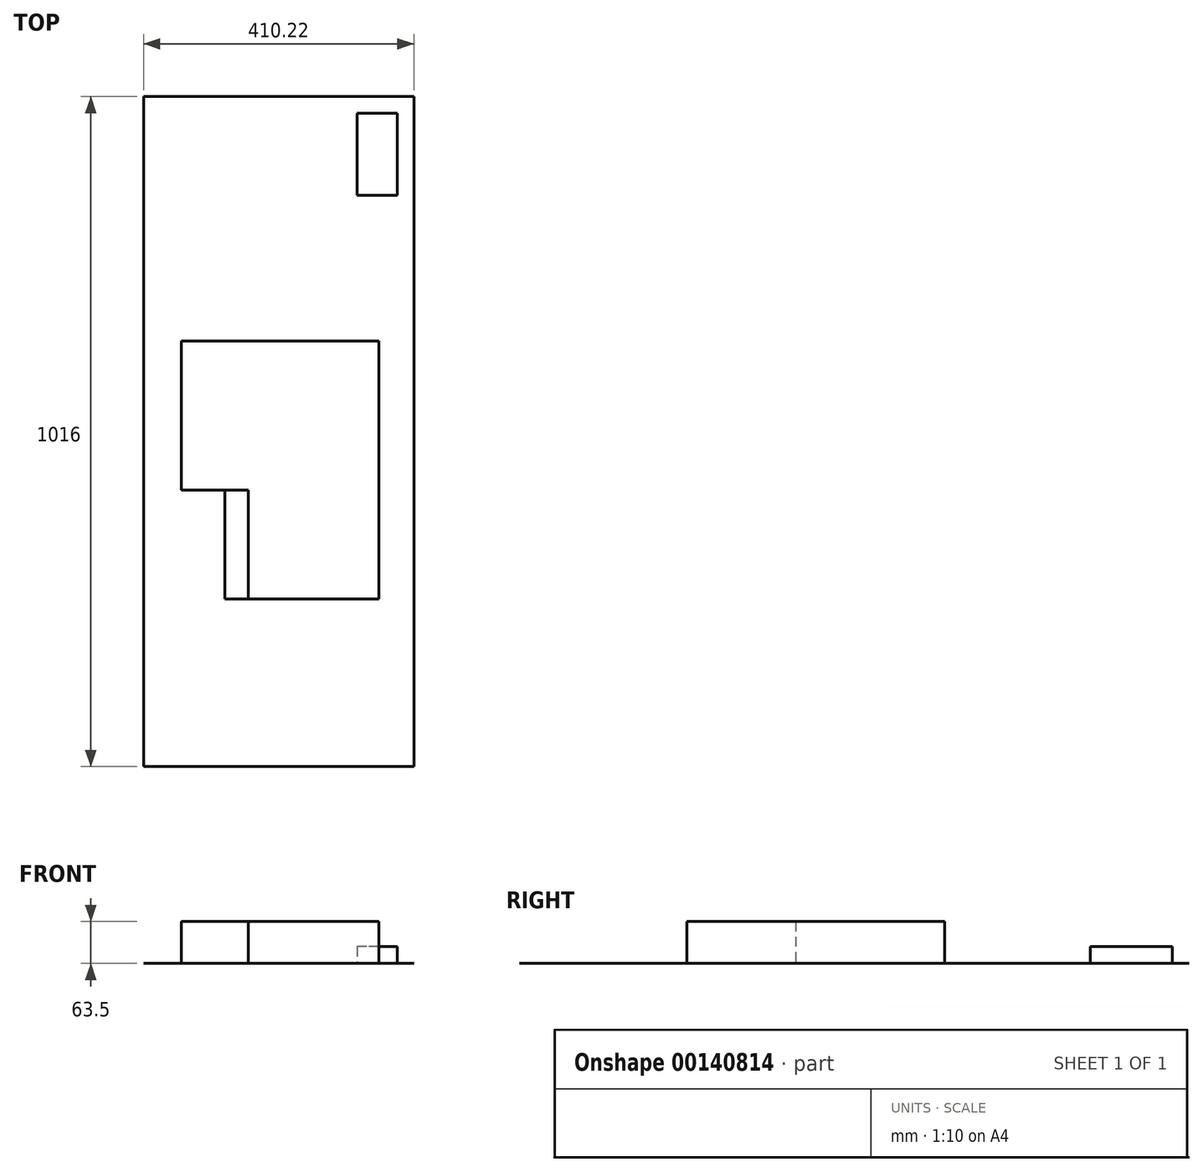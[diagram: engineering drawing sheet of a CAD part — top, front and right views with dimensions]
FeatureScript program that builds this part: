
annotation { "Feature Type Name" : "Feature", "Feature Type Description" : "" }
export const myFeature = defineFeature(function(context is Context, id is Id, definition is map)
    precondition{}
    {
        {
            var Q0;
            Q0=qCreatedBy(makeId("Top.planeOp"),FACE);
            var sketch = newSketch(context, id + "F0", { "sketchPlane" : qUnion([Q0])});
            skLineSegment(sketch, "E0.bottom", {"start": v(-205.1, 508) * mm, "end": v(205.1, 508) * mm});
            skLineSegment(sketch, "E0.top", {"start": v(-205.1, -508) * mm, "end": v(205.1, -508) * mm});
            skLineSegment(sketch, "E0.left", {"start": v(-205.1, 508) * mm, "end": v(-205.1, -508) * mm});
            skLineSegment(sketch, "E0.right", {"start": v(205.1, 508) * mm, "end": v(205.1, -508) * mm});
            skPoint(sketch, "E0.middle", {"position": v(0, 0) * mm});
            skSolve(sketch);
        }
        {
            var Q0;
            Q0=makeQuery(id+"F0.imprint","IMPRINT",FACE,{"disambiguationData":[TD([[makeQuery(id+"F0.imprint","IMPRINT",EDGE,{"derivedFrom":sQuery(id+"F0.wireOp",EDGE,"E0.bottom")}),-1.0]])]});
            var sketch = newSketch(context, id + "F1", { "sketchPlane" : qUnion([Q0])});
            skLineSegment(sketch, "E1.bottom", {"start": v(205.1, 508) * mm, "end": v(151.77, 508) * mm});
            skLineSegment(sketch, "E1.top", {"start": v(205.1, 137.16) * mm, "end": v(151.77, 137.16) * mm});
            skLineSegment(sketch, "E1.left", {"start": v(205.1, 508) * mm, "end": v(205.1, 137.16) * mm});
            skLineSegment(sketch, "E1.right", {"start": v(151.77, 508) * mm, "end": v(151.77, 137.16) * mm});
            skLineSegment(sketch, "E2.bottom", {"start": v(-205.1, 508) * mm, "end": v(-147.95, 508) * mm});
            skLineSegment(sketch, "E2.top", {"start": v(-205.1, 137.16) * mm, "end": v(-147.95, 137.16) * mm});
            skLineSegment(sketch, "E2.left", {"start": v(-205.1, 508) * mm, "end": v(-205.1, 137.16) * mm});
            skLineSegment(sketch, "E2.right", {"start": v(-147.95, 508) * mm, "end": v(-147.95, 137.16) * mm});
            skSolve(sketch);
        }
        {
            var Q0;
            Q0=makeQuery(id+"F0.imprint","IMPRINT",FACE,{"disambiguationData":[TD([[makeQuery(id+"F0.imprint","IMPRINT",EDGE,{"derivedFrom":sQuery(id+"F0.wireOp",EDGE,"E0.bottom")}),-1.0]])]});
            var sketch = newSketch(context, id + "F2", { "sketchPlane" : qUnion([Q0])});
            skLineSegment(sketch, "E3.bottom", {"start": v(151.77, 137.16) * mm, "end": v(-147.95, 137.16) * mm});
            skLineSegment(sketch, "E3.top", {"start": v(151.77, -254) * mm, "end": v(-147.95, -254) * mm});
            skLineSegment(sketch, "E3.left", {"start": v(151.77, 137.16) * mm, "end": v(151.77, -254) * mm});
            skLineSegment(sketch, "E3.right", {"start": v(-147.95, 137.16) * mm, "end": v(-147.95, -254) * mm});
            skLineSegment(sketch, "E4", {"start": v(151.77, -254) * mm, "end": v(-46.35, -254) * mm});
            skLineSegment(sketch, "E5", {"start": v(-46.35, -254) * mm, "end": v(-46.35, -88.9) * mm});
            skLineSegment(sketch, "E6", {"start": v(-46.35, -88.9) * mm, "end": v(-147.95, -88.9) * mm});
            skLineSegment(sketch, "E7", {"start": v(-81.91, -88.9) * mm, "end": v(-81.91, -254) * mm});
            skLineSegment(sketch, "E8", {"start": v(-81.91, -88.9) * mm, "end": v(-46.35, -88.9) * mm});
            skLineSegment(sketch, "E9", {"start": v(-46.35, -254) * mm, "end": v(-46.35, -508) * mm});
            skLineSegment(sketch, "E10", {"start": v(151.77, -254) * mm, "end": v(151.77, -508) * mm});
            skLineSegment(sketch, "E11", {"start": v(-46.35, -254) * mm, "end": v(-46.35, -299.72) * mm});
            skLineSegment(sketch, "E12", {"start": v(-46.35, -299.72) * mm, "end": v(-81.91, -254) * mm});
            skLineSegment(sketch, "E13", {"start": v(151.77, -254) * mm, "end": v(151.77, -299.72) * mm});
            skLineSegment(sketch, "E14", {"start": v(151.77, -299.72) * mm, "end": v(187.33, -254) * mm});
            skLineSegment(sketch, "E15", {"start": v(187.33, -254) * mm, "end": v(187.33, -79.8) * mm});
            skLineSegment(sketch, "E16", {"start": v(187.33, -79.8) * mm, "end": v(151.77, -79.8) * mm});
            skSolve(sketch);
        }
        {
            var Q0;
            {var subQ1=sQuery(id+"F2.wireOp",EDGE,"E3.bottom");Q0=makeQuery(id+"F2.imprint","IMPRINT",FACE,{"disambiguationData":[TD([[makeQuery(id+"F2.imprint","IMPRINT",EDGE,{"derivedFrom":subQ1}),1.0]])]});}
            extrude(context, id + "F3", {"entities" : qUnion([Q0]), "depth" : 63.5 * mm});
        }
        {
            var Q0;
            {var subQ0=sQuery(id+"F2.wireOp",EDGE,"E5");Q0=makeQuery(id+"F2.imprint","IMPRINT",FACE,{"disambiguationData":[TD([[makeQuery(id+"F2.imprint","IMPRINT",EDGE,{"derivedFrom":subQ0}),1.0]])]});}
            var Q1;
            {var subQ0=sQuery(id+"F2.wireOp",EDGE,"E11");Q1=makeQuery(id+"F2.imprint","IMPRINT",FACE,{"disambiguationData":[TD([[makeQuery(id+"F2.imprint","IMPRINT",EDGE,{"derivedFrom":subQ0}),-1.0]])]});}
            var Q2;
            Q2=makeQuery(id+"F2.imprint","IMPRINT",FACE,{"disambiguationData":[TD([[makeQuery(id+"F2.imprint","IMPRINT",EDGE,{"derivedFrom":sQuery(id+"F2.wireOp",EDGE,"E4")}),1.0]])]});
            var Q3;
            {var subQ0=sQuery(id+"F2.wireOp",EDGE,"E13");Q3=makeQuery(id+"F2.imprint","IMPRINT",FACE,{"disambiguationData":[TD([[makeQuery(id+"F2.imprint","IMPRINT",EDGE,{"derivedFrom":subQ0}),1.0]])]});}
            extrude(context, id + "F4", {"entities" : qUnion([Q0, Q1, Q2, Q3]), "depth" : 0.5 * mm});
        }
        {
            var Q0;
            Q0=makeQuery(id+"F0.imprint","IMPRINT",FACE,{"disambiguationData":[TD([[makeQuery(id+"F0.imprint","IMPRINT",EDGE,{"derivedFrom":sQuery(id+"F0.wireOp",EDGE,"E0.bottom")}),-1.0]])]});
            extrude(context, id + "F5", {"entities" : qUnion([Q0]), "depth" : 0.25 * mm});
        }
        {
            var Q0;
            Q0=makeQuery(id+"F5.opExtrude","CAP_FACE",FACE,{"disambiguationData":[OSD([sQuery(id+"F0.wireOp",EDGE,"E0.bottom"),sQuery(id+"F0.wireOp",EDGE,"E0.top"),sQuery(id+"F0.wireOp",EDGE,"E0.left"),sQuery(id+"F0.wireOp",EDGE,"E0.right")])],"isStart":false});
            var sketch = newSketch(context, id + "F6", { "sketchPlane" : qUnion([Q0])});
            skLineSegment(sketch, "E17.bottom", {"start": v(205.1, 508) * mm, "end": v(179.7, 508) * mm});
            skLineSegment(sketch, "E17.top", {"start": v(205.1, 482.6) * mm, "end": v(179.7, 482.6) * mm});
            skLineSegment(sketch, "E17.left", {"start": v(205.1, 508) * mm, "end": v(205.1, 482.6) * mm});
            skLineSegment(sketch, "E17.right", {"start": v(179.7, 508) * mm, "end": v(179.7, 482.6) * mm});
            skLineSegment(sketch, "E18.bottom", {"start": v(179.7, 482.6) * mm, "end": v(118.75, 482.6) * mm});
            skLineSegment(sketch, "E18.top", {"start": v(179.7, 358.14) * mm, "end": v(118.75, 358.14) * mm});
            skLineSegment(sketch, "E18.left", {"start": v(179.7, 482.6) * mm, "end": v(179.7, 358.14) * mm});
            skLineSegment(sketch, "E18.right", {"start": v(118.75, 482.6) * mm, "end": v(118.75, 358.14) * mm});
            skSolve(sketch);
        }
        {
            var Q0;
            Q0=makeQuery(id+"F6.imprint","IMPRINT",FACE,{"disambiguationData":[TD([[makeQuery(id+"F6.imprint","IMPRINT",EDGE,{"derivedFrom":sQuery(id+"F6.wireOp",EDGE,"E18.bottom")}),1.0]])]});
            extrude(context, id + "F7", {"entities" : qUnion([Q0]), "depth" : 25.4 * mm});
        }
    });
